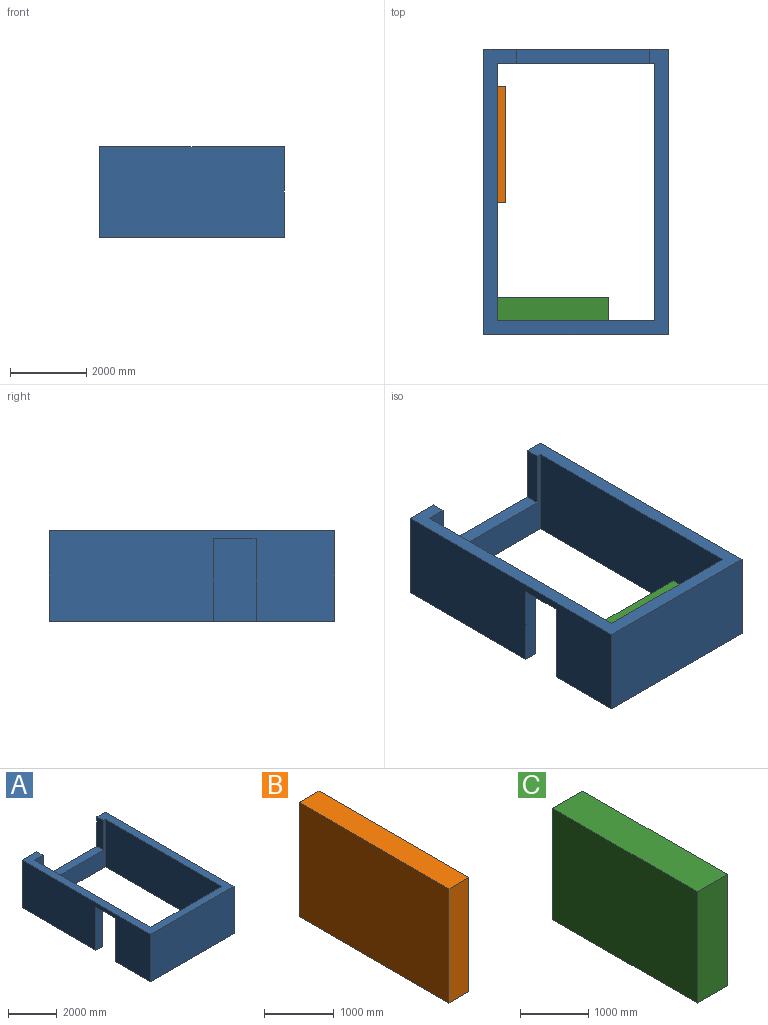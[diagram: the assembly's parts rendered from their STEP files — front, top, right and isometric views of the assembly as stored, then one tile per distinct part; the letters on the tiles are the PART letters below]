
ASSEMBLY  parts=3 mates=2
PART A: 16 faces, bbox 4850x7500x2390 mm
  f0: plane 7500x2390mm, normal (-1,0,0), area 15461600mm2, adj f7,f8,f10,f11,f12,f13,f14
  f1: plane 1490x365mm, normal (-1,0,0), area 543850mm2, adj f5,f7,f10,f15
  f2: plane 6770x2390mm, normal (-1,0,0), area 16180300mm2, adj f3,f5,f10,f11
  f3: plane 4120x2390mm, normal (0,1,0), area 9846800mm2, adj f2,f4,f10,f11
  f4: plane 6770x2390mm, normal (1,0,0), area 13716900mm2, adj f3,f5,f10,f11,f12,f13,f14
  f5: plane 4120x2390mm, normal (0,-1,0), area 4631800mm2, adj f1,f2,f4,f6,f10,f11,f15
  f6: plane 1490x365mm, normal (1,0,0), area 543850mm2, adj f5,f7,f10,f15
  f7: plane 4850x2390mm, normal (0,1,0), area 6376500mm2, adj f0,f1,f6,f9,f10,f11,f15
  f8: plane 4850x2390mm, normal (0,-1,0), area 11591500mm2, adj f0,f9,f10,f11
  f9: plane 7500x2390mm, normal (1,0,0), area 17925000mm2, adj f7,f8,f10,f11
  f10: plane 7500x4850mm, normal (0,0,1), area 7205100mm2, adj f0,f1,f2,f3,f4,f5,f6,f7
  f11: plane 7500x4850mm, normal (0,0,-1), area 8070150mm2, adj f0,f2,f3,f4,f5,f7,f8,f9
  f12: plane 2180x365mm, normal (0,1,0), area 795700mm2, adj f0,f4,f11,f14
  f13: plane 2180x365mm, normal (0,-1,0), area 795700mm2, adj f0,f4,f11,f14
  f14: plane 1130x365mm, normal (0,0,-1), area 412450mm2, adj f0,f4,f12,f13
  f15: plane 3500x365mm, normal (0,0,1), area 1277500mm2, adj f1,f5,f6,f7
PART B: 6 faces, bbox 400x3030x2000 mm
  f0: plane 3030x2000mm, normal (-1,0,0), area 6060000mm2, adj f1,f3,f4,f5
  f1: plane 2000x400mm, normal (0,-1,0), area 800000mm2, adj f0,f2,f4,f5
  f2: plane 3030x2000mm, normal (1,0,0), area 6060000mm2, adj f1,f3,f4,f5
  f3: plane 2000x400mm, normal (0,1,0), area 800000mm2, adj f0,f2,f4,f5
  f4: plane 3030x400mm, normal (0,0,1), area 1212000mm2, adj f0,f1,f2,f3
  f5: plane 3030x400mm, normal (0,0,-1), area 1212000mm2, adj f0,f1,f2,f3
PART C: 6 faces, bbox 624x3000x2000 mm
  f0: plane 3000x2000mm, normal (-1,0,0), area 6000000mm2, adj f1,f3,f4,f5
  f1: plane 2000x624mm, normal (0,-1,0), area 1248000mm2, adj f0,f2,f4,f5
  f2: plane 3000x2000mm, normal (1,0,0), area 6000000mm2, adj f1,f3,f4,f5
  f3: plane 2000x624mm, normal (0,1,0), area 1248000mm2, adj f0,f2,f4,f5
  f4: plane 3000x624mm, normal (0,0,1), area 1872000mm2, adj f0,f1,f2,f3
  f5: plane 3000x624mm, normal (0,0,-1), area 1872000mm2, adj f0,f1,f2,f3
PLACE A t=(-6075.45,4107.48,-10102.47)mm
PLACE B t=(-17420.76,9317.68,-10102.47)mm
PLACE C rot(axis=(0,0,1),90deg) t=(-15043.45,-3468.71,-10102.47)mm
MATE planar B.f5 <-> A.f11  axis (0,0,-1) through (-10086.42,8740.85,-10102.47)mm
MATE planar C.f5 <-> A.f11  axis (0,0,-1) through (-8471.86,4102.32,-10102.47)mm
